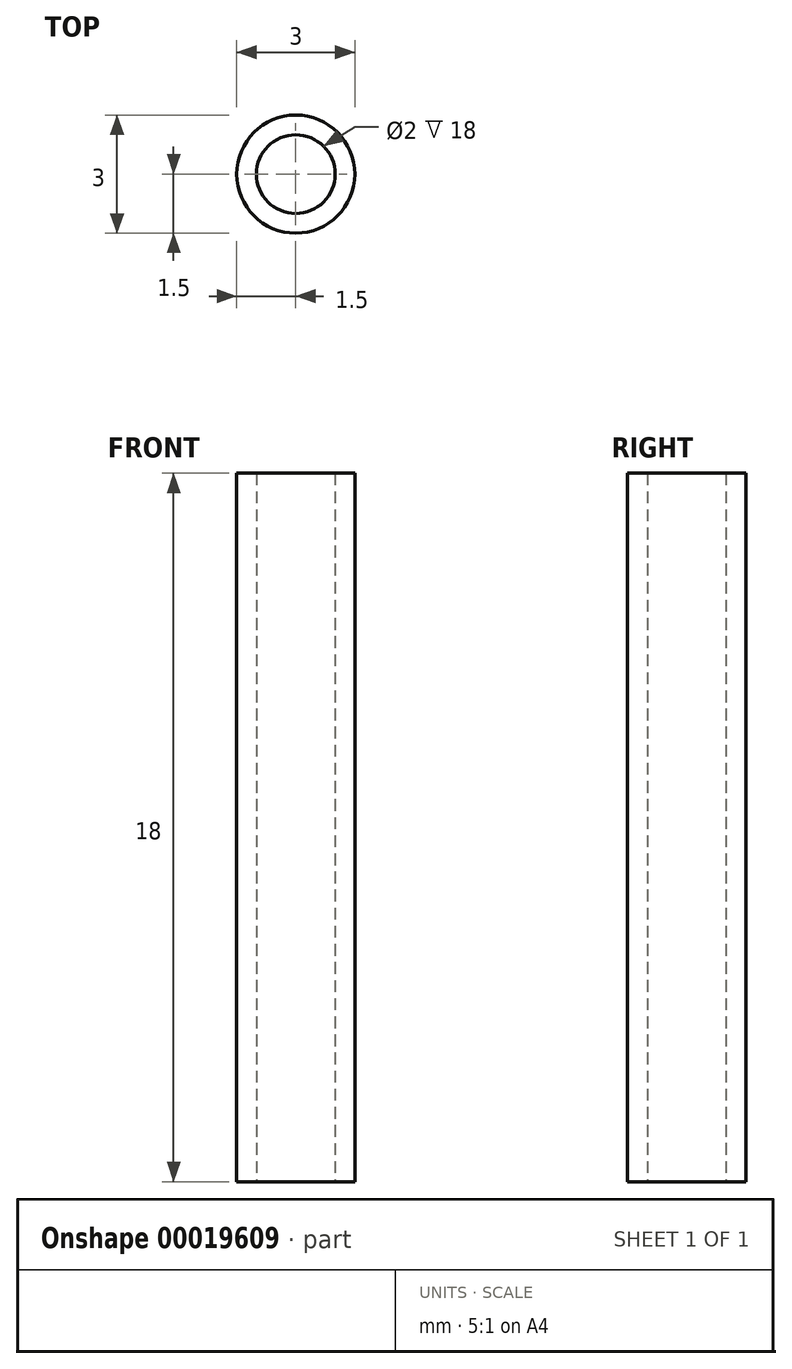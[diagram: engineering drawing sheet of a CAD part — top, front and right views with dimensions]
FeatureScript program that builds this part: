
annotation { "Feature Type Name" : "Feature", "Feature Type Description" : "" }
export const myFeature = defineFeature(function(context is Context, id is Id, definition is map)
    precondition{}
    {
        {
            var Q0;
            Q0=qCreatedBy(makeId("Top.planeOp"),FACE);
            var sketch = newSketch(context, id + "F0", { "sketchPlane" : qUnion([Q0])});
            skCircle(sketch, "E0", {"center": v(0, 0) * mm, "radius": 1.5 * mm});
            skCircle(sketch, "E1", {"center": v(0, 0) * mm, "radius": 1 * mm});
            skSolve(sketch);
        }
        {
            var Q0;
            Q0=makeQuery(id+"F0.imprint","IMPRINT",FACE,{"disambiguationData":[TD([[makeQuery(id+"F0.imprint","IMPRINT",EDGE,{"derivedFrom":sQuery(id+"F0.wireOp",EDGE,"E0")}),1.0]])]});
            extrude(context, id + "F1", {"entities" : qUnion([Q0]), "depth" : 18 * mm});
        }
    });
